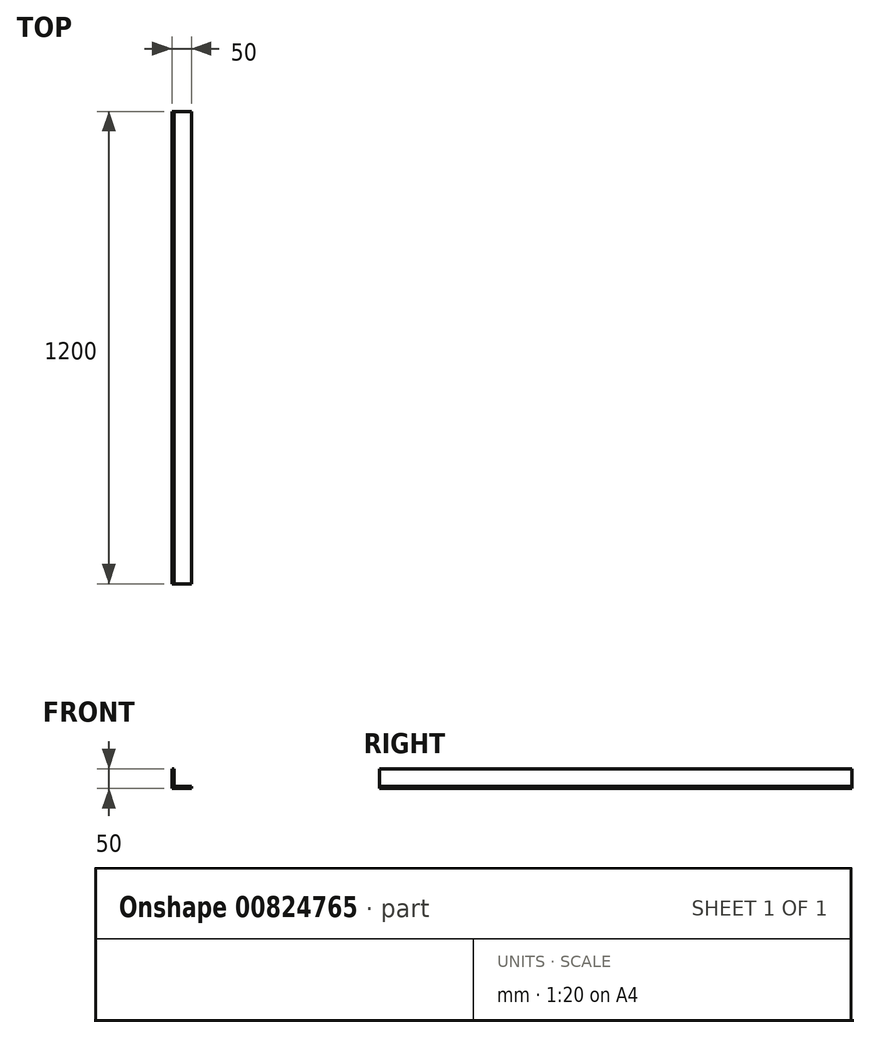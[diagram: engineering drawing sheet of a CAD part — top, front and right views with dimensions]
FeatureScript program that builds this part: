
annotation { "Feature Type Name" : "Feature", "Feature Type Description" : "" }
export const myFeature = defineFeature(function(context is Context, id is Id, definition is map)
    precondition{}
    {
        {
            var Q0;
            Q0=qCreatedBy(makeId("Front.planeOp"),FACE);
            var sketch = newSketch(context, id + "F0", { "sketchPlane" : qUnion([Q0])});
            skLineSegment(sketch, "E0", {"start": v(0, 0) * mm, "end": v(0, 50) * mm});
            skLineSegment(sketch, "E1", {"start": v(0, 50) * mm, "end": v(5, 50) * mm});
            skLineSegment(sketch, "E2", {"start": v(5, 50) * mm, "end": v(5, 5) * mm});
            skLineSegment(sketch, "E3", {"start": v(5, 5) * mm, "end": v(50, 5) * mm});
            skLineSegment(sketch, "E4", {"start": v(50, 5) * mm, "end": v(50, 0) * mm});
            skLineSegment(sketch, "E5", {"start": v(50, 0) * mm, "end": v(0, 0) * mm});
            skSolve(sketch);
        }
        {
            var Q0;
            Q0=makeQuery(id+"F0.imprint","IMPRINT",FACE,{"disambiguationData":[TD([[makeQuery(id+"F0.imprint","IMPRINT",EDGE,{"derivedFrom":sQuery(id+"F0.wireOp",EDGE,"E0")}),-1.0]])]});
            extrude(context, id + "F1", {"entities" : qUnion([Q0]), "depth" : 1200 * mm, "offsetDistance" : 25 * mm});
        }
        {
            var Q0;
            Q0=makeQuery(id+"F1.opExtrude","SWEPT_FACE",FACE,{"disambiguationData":[OSD([sQuery(id+"F0.wireOp",EDGE,"E2")])]});
            var sketch = newSketch(context, id + "F2", { "sketchPlane" : qUnion([Q0])});
            skLineSegment(sketch, "E6", {"start": v(-600, 50) * mm, "end": v(-600, 32) * mm});
            skLineSegment(sketch, "E7", {"start": v(-600, 32) * mm, "end": v(-453.5, 32) * mm});
            skLineSegment(sketch, "E8", {"start": v(-600, 32) * mm, "end": v(-748.15, 32) * mm});
            skCircle(sketch, "E9", {"center": v(-748.15, 32) * mm, "radius": 5 * mm});
            skCircle(sketch, "E10", {"center": v(-453.5, 32) * mm, "radius": 5 * mm});
            skSolve(sketch);
        }
        {
            var Q0;
            Q0=makeQuery(id+"F1.opExtrude","SWEPT_FACE",FACE,{"disambiguationData":[OSD([sQuery(id+"F0.wireOp",EDGE,"E3")])]});
            var sketch = newSketch(context, id + "F3", { "sketchPlane" : qUnion([Q0])});
            skLineSegment(sketch, "E11", {"start": v(50, 0) * mm, "end": v(50, -20) * mm});
            skCircle(sketch, "E12", {"center": v(40, -20) * mm, "radius": 3 * mm});
            skSolve(sketch);
        }
    });
